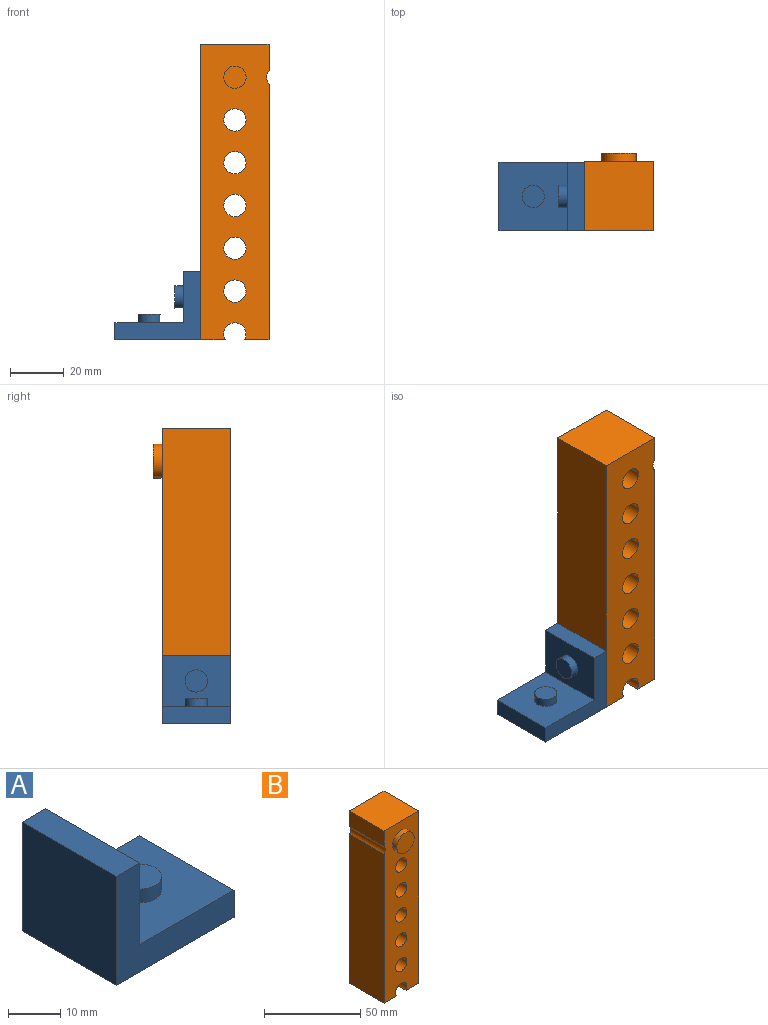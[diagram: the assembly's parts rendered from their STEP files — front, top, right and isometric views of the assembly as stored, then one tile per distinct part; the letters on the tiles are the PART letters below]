
ASSEMBLY  parts=2 mates=1
PART A: 12 faces, bbox 31.8x25.4x25.4 mm
  f0: plane 25.4x25.4mm, normal (-1,0,0), area 645.2mm2, adj f1,f3,f4,f5
  f1: plane 31.75x25.4mm, normal (0,1,0), area 322.6mm2, adj f0,f2,f4,f5,f6,f7
  f2: plane 25.4x19.05mm, normal (1,0,0), area 430.3mm2, adj f1,f3,f4,f6,f10
  f3: plane 31.75x25.4mm, normal (0,-1,0), area 322.6mm2, adj f0,f2,f4,f5,f6,f7
  f4: plane 25.4x6.35mm, normal (0,0,1), area 161.3mm2, adj f0,f1,f2,f3
  f5: plane 31.75x25.4mm, normal (0,0,-1), area 806.5mm2, adj f0,f1,f3,f7
  f6: plane 25.4x25.4mm, normal (0,0,1), area 591.6mm2, adj f1,f2,f3,f7,f8
  f7: plane 25.4x6.35mm, normal (1,0,0), area 161.3mm2, adj f1,f3,f5,f6
  f8: cylinder r=4.13mm len=8.26mm, axis (0,0,-1), area 82.3mm2, adj f6,f9
  f9: plane 8.26x8.26mm, normal (0,0,1), area 53.5mm2, adj f8
  f10: cylinder r=4.13mm len=8.26mm, axis (-1,0,0), area 82.3mm2, adj f2,f11
  f11: plane 8.26x8.26mm, normal (1,0,0), area 53.5mm2, adj f10
PART B: 20 faces, bbox 25.4x28.6x109.6 mm
  f0: cylinder r=4.13mm len=25.4mm, axis (0,1,0), area 330.5mm2, adj f11,f16,f19
  f1: plane 25.4x25.4mm, normal (0,0,1), area 645.2mm2, adj f2,f13,f15,f16
  f2: plane 109.6x25.4mm, normal (1,0,0), area 2783.9mm2, adj f1,f3,f15,f16
  f3: plane 25.4x9.22mm, normal (0,0,-1), area 234.2mm2, adj f2,f4,f15,f16
  f4: cylinder r=4.13mm len=25.4mm, axis (0,1,0), area 445mm2, adj f3,f5,f15,f16
  f5: plane 25.4x9.15mm, normal (0,0,-1), area 232.3mm2, adj f4,f6,f15,f16
  f6: plane 94.8x25.4mm, normal (-1,0,0), area 2408mm2, adj f5,f7,f15,f16
  f7: cylinder r=4.13mm len=25.4mm, axis (0,1,0), area 140.9mm2, adj f6,f13,f15,f16
  f8: cylinder r=4.13mm len=25.4mm, axis (0,1,0), area 658.7mm2, adj f15,f16
  f9: cylinder r=4.13mm len=25.4mm, axis (0,1,0), area 658.7mm2, adj f15,f16
  f10: cylinder r=4.13mm len=25.4mm, axis (0,1,0), area 658.7mm2, adj f15,f16
  f11: cylinder r=4.13mm len=25.4mm, axis (0,1,0), area 330.5mm2, adj f0,f16,f19
  f12: cylinder r=4.13mm len=25.4mm, axis (0,1,0), area 658.7mm2, adj f15,f16
  f13: plane 25.4x9.66mm, normal (-1,0,0), area 245.3mm2, adj f1,f7,f15,f16
  f14: cylinder r=4.13mm len=25.4mm, axis (0,1,0), area 658.7mm2, adj f15,f16
  f15: plane 109.6x25.4mm, normal (0,-1,0), area 2342.7mm2, adj f1,f2,f3,f4,f5,f6,f7,f8
  f16: plane 109.6x25.4mm, normal (0,1,0), area 2415.5mm2, adj f0,f1,f2,f3,f4,f5,f6,f7
  f17: plane 12.7x12.7mm, normal (0,-1,0), area 126.7mm2, adj f18
  f18: cylinder r=6.35mm len=12.7mm, axis (0,1,0), area 126.7mm2, adj f15,f17
  f19: plane 8.3x8.27mm, normal (0,1,0), area 53.9mm2, adj f0,f11
PLACE A rot(axis=(0,0,1),180deg) t=(127.03,0,0)mm
PLACE B rot(axis=(0,0,1),180deg) t=(127.03,0,0)mm fixed
MATE fastened B.f2 <-> A.f0  axis (-1,0,0) through (50.82,127,0)mm
